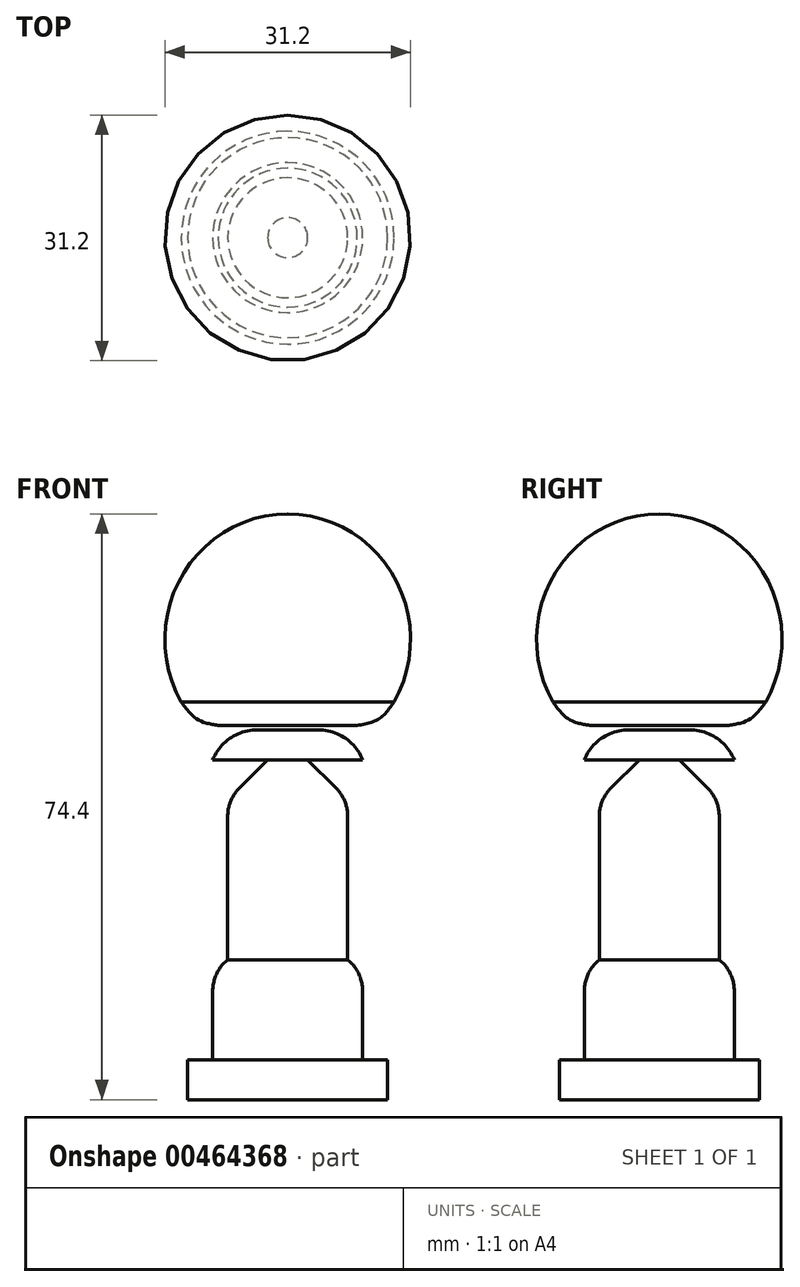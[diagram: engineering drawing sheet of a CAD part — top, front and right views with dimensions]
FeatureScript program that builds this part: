
annotation { "Feature Type Name" : "Feature", "Feature Type Description" : "" }
export const myFeature = defineFeature(function(context is Context, id is Id, definition is map)
    precondition{}
    {
        {
            var Q0;
            Q0=qCreatedBy(makeId("Top.planeOp"),FACE);
            var sketch = newSketch(context, id + "F0", { "sketchPlane" : qUnion([Q0])});
            skCircle(sketch, "E0", {"center": v(0, 0) * mm, "radius": 12.7 * mm});
            skSolve(sketch);
        }
        {
            var Q0;
            Q0 = qSketchRegion(id + "F0", true);
            extrude(context, id + "F1", {"entities" : qUnion([Q0]), "depth" : 5.08 * mm});
        }
        {
            var Q0;
            Q0=makeQuery(id+"F1.opExtrude","CAP_FACE",FACE,{"disambiguationData":[OSD([sQuery(id+"F0.wireOp",EDGE,"E0")])],"isStart":false});
            var sketch = newSketch(context, id + "F2", { "sketchPlane" : qUnion([Q0])});
            skCircle(sketch, "E1", {"center": v(0, 0) * mm, "radius": 9.53 * mm});
            skSolve(sketch);
        }
        {
            var Q0;
            Q0 = qSketchRegion(id + "F2", true);
            extrude(context, id + "F3", {"entities" : qUnion([Q0]), "operationType" : NewBodyOperationType.ADD, "depth" : 12.7 * mm});
        }
        {
            var Q0;
            Q0=makeQuery(id+"F3.opExtrude","CAP_FACE",FACE,{"disambiguationData":[OSD([sQuery(id+"F2.wireOp",EDGE,"E1")])],"isStart":false});
            var sketch = newSketch(context, id + "F4", { "sketchPlane" : qUnion([Q0])});
            skCircle(sketch, "E2", {"center": v(0, 0) * mm, "radius": 7.62 * mm});
            skSolve(sketch);
        }
        {
            var Q0;
            Q0 = qSketchRegion(id + "F4", true);
            extrude(context, id + "F5", {"entities" : qUnion([Q0]), "operationType" : NewBodyOperationType.ADD, "depth" : 25.4 * mm});
        }
        {
            var Q0;
            Q0=makeQuery(id+"F3.opExtrude","CAP_EDGE",EDGE,{"disambiguationData":[OSD([sQuery(id+"F2.wireOp",EDGE,"E1")])],"isStart":false});
            fillet(context, id + "F6", {"entities" : qUnion([Q0]), "radius" : 5.08 * mm, "tangentPropagation" : true, "allowEdgeOverflow" : false});
        }
        {
            var Q0;
            Q0=makeQuery(id+"F5.opExtrude","CAP_EDGE",EDGE,{"disambiguationData":[OSD([sQuery(id+"F4.wireOp",EDGE,"E2")])],"isStart":false});
            chamfer(context, id + "F7", {"entities" : qUnion([Q0]), "width" : 5.08 * mm, "tangentPropagation" : true});
        }
        {
            var Q0;
            {var subQ0=sQuery(id+"F4.wireOp",EDGE,"E2");Q0=makeQuery(id+"F7.opChamfer","BLEND_EDGE",EDGE,{"blendedFrom":[makeQuery(id+"F5.opExtrude","CAP_EDGE",EDGE,{"disambiguationData":[OSD([subQ0])],"isStart":false}),makeQuery(id+"F5.opExtrude","SWEPT_FACE",FACE,{"disambiguationData":[OSD([subQ0])]})],"blendedInto":[makeQuery(id+"F5.opExtrude","SWEPT_FACE",FACE,{"disambiguationData":[OSD([subQ0])]})]});}
            fillet(context, id + "F8", {"entities" : qUnion([Q0]), "radius" : 5.08 * mm, "tangentPropagation" : true, "allowEdgeOverflow" : false});
        }
        {
            var Q0;
            Q0=makeQuery(id+"F5.opExtrude","CAP_FACE",FACE,{"disambiguationData":[OSD([sQuery(id+"F4.wireOp",EDGE,"E2")])],"isStart":false});
            var sketch = newSketch(context, id + "F9", { "sketchPlane" : qUnion([Q0])});
            skCircle(sketch, "E3", {"center": v(0, 0) * mm, "radius": 9.53 * mm});
            skSolve(sketch);
        }
        {
            var Q0;
            Q0 = qSketchRegion(id + "F9", true);
            extrude(context, id + "F10", {"entities" : qUnion([Q0]), "operationType" : NewBodyOperationType.ADD, "depth" : 3.8 * mm});
        }
        {
            var Q0;
            Q0=makeQuery(id+"F10.opExtrude","CAP_EDGE",EDGE,{"disambiguationData":[OSD([sQuery(id+"F9.wireOp",EDGE,"E3")])],"isStart":false});
            fillet(context, id + "F11", {"entities" : qUnion([Q0]), "radius" : 6.13 * mm, "tangentPropagation" : true, "allowEdgeOverflow" : false});
        }
        {
            var Q0;
            Q0=qCreatedBy(makeId("Right.planeOp"),FACE);
            var sketch = newSketch(context, id + "F12", { "sketchPlane" : qUnion([Q0])});
            skEllipse(sketch, "E4", {"center": v(0, 58.47) * mm, "majorRadius": 15.93 * mm, "minorRadius": 15.6 * mm, "majorAxis": v(0, -1)});
            skLineSegment(sketch, "E5", {"start": v(11.35, 47.54) * mm, "end": v(-11.35, 47.54) * mm});
            skFitSpline(sketch, "E6", {"points": [v(12.84, 49.43) * mm, v(11.35, 47.54) * mm], "startDerivative": vector(-1.48, -1.9) * mm, "endDerivative": vector(-1.48, -1.9) * mm});
            skFitSpline(sketch, "E7", {"points": [v(13.52, 50.53) * mm, v(11.52, 48.34) * mm, v(8.82, 47.54) * mm], "startDerivative": vector(-3.56, -5) * mm, "endDerivative": vector(-5.83, -0.96) * mm});
            skFitSpline(sketch, "E8.MirrorCS", {"points": [v(-13.52, 50.53) * mm, v(-11.52, 48.34) * mm, v(-8.82, 47.54) * mm], "startDerivative": vector(3.56, -5) * mm, "endDerivative": vector(5.83, -0.96) * mm});
            skLineSegment(sketch, "E9", {"start": v(0, 76.03) * mm, "end": v(0, -4.83) * mm});
            skPoint(sketch, "E9.endSnap0", {"position": v(0, 74.4) * mm});
            skSolve(sketch);
        }
        {
            var Q0;
            {var subQ0=sQuery(id+"F12.wireOp",EDGE,"E7");Q0=makeQuery(id+"F12.imprint","IMPRINT",FACE,{"disambiguationData":[TD([[makeQuery(id+"F12.imprint","IMPRINT",EDGE,{"derivedFrom":subQ0}),-1.0]])]});}
            var Q1;
            Q1=sQuery(id+"F12.wireOp",EDGE,"E9");
            revolve(context, id + "F13", {"entities" : qUnion([Q0]), "axis" : qUnion([Q1]), "revolveType" : RevolveType.FULL});
        }
    });
